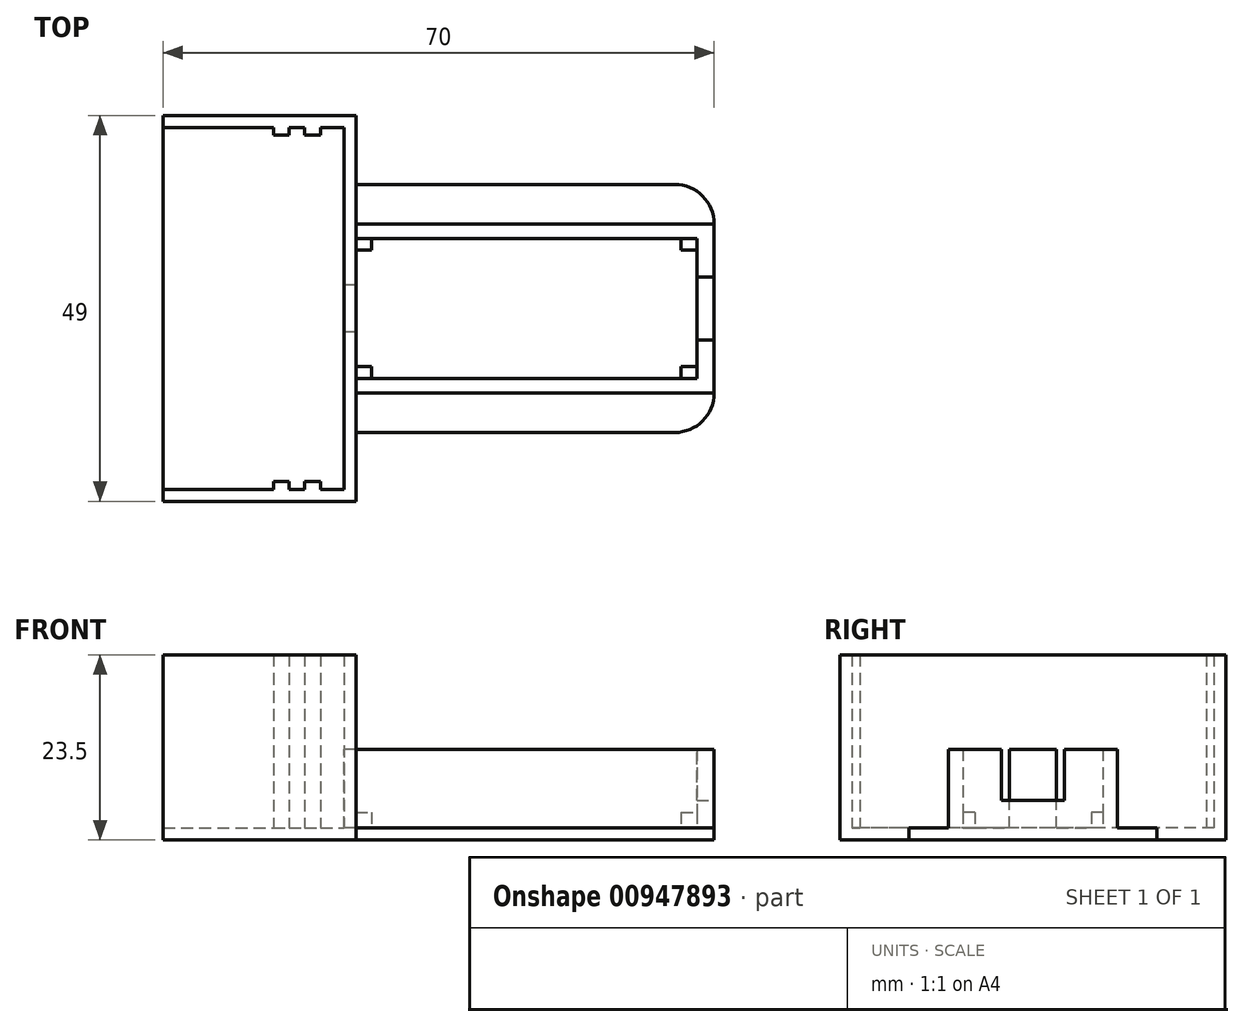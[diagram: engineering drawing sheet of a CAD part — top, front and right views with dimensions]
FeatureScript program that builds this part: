
annotation { "Feature Type Name" : "Feature", "Feature Type Description" : "" }
export const myFeature = defineFeature(function(context is Context, id is Id, definition is map)
    precondition{}
    {
        {
            var Q0;
            Q0=qCreatedBy(makeId("Top.planeOp"),FACE);
            var sketch = newSketch(context, id + "F0", { "sketchPlane" : qUnion([Q0])});
            skLineSegment(sketch, "E0.bottom", {"start": v(0, 24.5) * mm, "end": v(-23, 24.5) * mm});
            skLineSegment(sketch, "E0.top", {"start": v(0, -24.5) * mm, "end": v(-23, -24.5) * mm});
            skLineSegment(sketch, "E0.left", {"start": v(0, 24.5) * mm, "end": v(0, -24.5) * mm});
            skLineSegment(sketch, "E0.right", {"start": v(-23, 24.5) * mm, "end": v(-23, -24.5) * mm});
            skSolve(sketch);
        }
        {
            var Q0;
            Q0 = qSketchRegion(id + "F0", true);
            extrude(context, id + "F1", {"entities" : qUnion([Q0]), "depth" : 1.5 * mm, "offsetDistance" : 25 * mm});
        }
        {
            var Q0;
            Q0=makeQuery(id+"F1.opExtrude","CAP_FACE",FACE,{"disambiguationData":[OSD([sQuery(id+"F0.wireOp",EDGE,"E0.bottom"),sQuery(id+"F0.wireOp",EDGE,"E0.top"),sQuery(id+"F0.wireOp",EDGE,"E0.left"),sQuery(id+"F0.wireOp",EDGE,"E0.right")])],"isStart":false});
            var sketch = newSketch(context, id + "F2", { "sketchPlane" : qUnion([Q0])});
            skLineSegment(sketch, "E1.bottom", {"start": v(-23, 24.5) * mm, "end": v(0, 24.5) * mm});
            skLineSegment(sketch, "E1.top", {"start": v(-23, 23) * mm, "end": v(0, 23) * mm});
            skLineSegment(sketch, "E1.left", {"start": v(-23, 24.5) * mm, "end": v(-23, 23) * mm});
            skLineSegment(sketch, "E1.right", {"start": v(0, 24.5) * mm, "end": v(0, 23) * mm});
            skLineSegment(sketch, "E2.bottom", {"start": v(-23, -23) * mm, "end": v(0, -23) * mm});
            skLineSegment(sketch, "E2.top", {"start": v(-23, -24.5) * mm, "end": v(0, -24.5) * mm});
            skLineSegment(sketch, "E2.left", {"start": v(-23, -23) * mm, "end": v(-23, -24.5) * mm});
            skLineSegment(sketch, "E2.right", {"start": v(0, -23) * mm, "end": v(0, -24.5) * mm});
            skSolve(sketch);
        }
        {
            var Q0;
            Q0=makeQuery(id+"F2.imprint","IMPRINT",FACE,{"disambiguationData":[TD([[makeQuery(id+"F2.imprint","IMPRINT",EDGE,{"derivedFrom":sQuery(id+"F2.wireOp",EDGE,"E1.bottom")}),1.0]])]});
            var Q1;
            Q1=makeQuery(id+"F2.imprint","IMPRINT",FACE,{"disambiguationData":[TD([[makeQuery(id+"F2.imprint","IMPRINT",EDGE,{"derivedFrom":sQuery(id+"F2.wireOp",EDGE,"E2.bottom")}),-1.0]])]});
            extrude(context, id + "F3", {"entities" : qUnion([Q0, Q1]), "operationType" : NewBodyOperationType.ADD, "depth" : 22 * mm, "offsetDistance" : 25 * mm});
        }
        {
            var Q0;
            Q0=makeQuery(id+"F1.opExtrude","CAP_FACE",FACE,{"disambiguationData":[OSD([sQuery(id+"F0.wireOp",EDGE,"E0.bottom"),sQuery(id+"F0.wireOp",EDGE,"E0.top"),sQuery(id+"F0.wireOp",EDGE,"E0.left"),sQuery(id+"F0.wireOp",EDGE,"E0.right")])],"isStart":false});
            var sketch = newSketch(context, id + "F4", { "sketchPlane" : qUnion([Q0])});
            skLineSegment(sketch, "E3.bottom", {"start": v(-5, 23) * mm, "end": v(-3, 23) * mm});
            skLineSegment(sketch, "E3.top", {"start": v(-5, 22) * mm, "end": v(-3, 22) * mm});
            skLineSegment(sketch, "E3.left", {"start": v(-5, 23) * mm, "end": v(-5, 22) * mm});
            skLineSegment(sketch, "E3.right", {"start": v(-3, 23) * mm, "end": v(-3, 22) * mm});
            skLineSegment(sketch, "E4.bottom", {"start": v(-3, -23) * mm, "end": v(-5, -23) * mm});
            skLineSegment(sketch, "E4.top", {"start": v(-3, -22) * mm, "end": v(-5, -22) * mm});
            skLineSegment(sketch, "E4.left", {"start": v(-3, -23) * mm, "end": v(-3, -22) * mm});
            skLineSegment(sketch, "E4.right", {"start": v(-5, -23) * mm, "end": v(-5, -22) * mm});
            skLineSegment(sketch, "E5.bottom", {"start": v(-7, -23) * mm, "end": v(-9, -23) * mm});
            skLineSegment(sketch, "E5.top", {"start": v(-7, -22) * mm, "end": v(-9, -22) * mm});
            skLineSegment(sketch, "E5.left", {"start": v(-7, -23) * mm, "end": v(-7, -22) * mm});
            skLineSegment(sketch, "E5.right", {"start": v(-9, -23) * mm, "end": v(-9, -22) * mm});
            skLineSegment(sketch, "E6.bottom", {"start": v(-9, 23) * mm, "end": v(-7, 23) * mm});
            skLineSegment(sketch, "E6.top", {"start": v(-9, 22) * mm, "end": v(-7, 22) * mm});
            skLineSegment(sketch, "E6.left", {"start": v(-9, 23) * mm, "end": v(-9, 22) * mm});
            skLineSegment(sketch, "E6.right", {"start": v(-7, 23) * mm, "end": v(-7, 22) * mm});
            skSolve(sketch);
        }
        {
            var Q0;
            Q0=makeQuery(id+"F4.imprint","IMPRINT",FACE,{"disambiguationData":[TD([[makeQuery(id+"F4.imprint","IMPRINT",EDGE,{"derivedFrom":sQuery(id+"F4.wireOp",EDGE,"E3.bottom")}),-1.0]])]});
            var Q1;
            Q1=makeQuery(id+"F4.imprint","IMPRINT",FACE,{"disambiguationData":[TD([[makeQuery(id+"F4.imprint","IMPRINT",EDGE,{"derivedFrom":sQuery(id+"F4.wireOp",EDGE,"E5.bottom")}),1.0]])]});
            var Q2;
            Q2=makeQuery(id+"F4.imprint","IMPRINT",FACE,{"disambiguationData":[TD([[makeQuery(id+"F4.imprint","IMPRINT",EDGE,{"derivedFrom":sQuery(id+"F4.wireOp",EDGE,"E4.bottom")}),1.0]])]});
            var Q3;
            Q3=makeQuery(id+"F4.imprint","IMPRINT",FACE,{"disambiguationData":[TD([[makeQuery(id+"F4.imprint","IMPRINT",EDGE,{"derivedFrom":sQuery(id+"F4.wireOp",EDGE,"E6.bottom")}),-1.0]])]});
            extrude(context, id + "F5", {"entities" : qUnion([Q0, Q1, Q2, Q3]), "operationType" : NewBodyOperationType.ADD, "depth" : 22 * mm, "offsetDistance" : 25 * mm});
        }
        {
            var Q0;
            Q0=qCreatedBy(makeId("Top.planeOp"),FACE);
            var sketch = newSketch(context, id + "F6", { "sketchPlane" : qUnion([Q0])});
            skLineSegment(sketch, "E7.bottom", {"start": v(0, 10.75) * mm, "end": v(47, 10.75) * mm});
            skLineSegment(sketch, "E7.top", {"start": v(0, -10.75) * mm, "end": v(47, -10.75) * mm});
            skLineSegment(sketch, "E7.left", {"start": v(0, 10.75) * mm, "end": v(0, -10.75) * mm});
            skLineSegment(sketch, "E7.right", {"start": v(47, 10.75) * mm, "end": v(47, -10.75) * mm});
            skSolve(sketch);
        }
        {
            var Q0;
            Q0 = qSketchRegion(id + "F6", true);
            extrude(context, id + "F7", {"entities" : qUnion([Q0]), "operationType" : NewBodyOperationType.ADD, "depth" : 1.5 * mm, "offsetDistance" : 25 * mm});
        }
        {
            var Q0;
            Q0=qCreatedBy(makeId("Top.planeOp"),FACE);
            var sketch = newSketch(context, id + "F8", { "sketchPlane" : qUnion([Q0])});
            skLineSegment(sketch, "E8.bottom", {"start": v(0, 24.5) * mm, "end": v(1.5, 24.5) * mm});
            skLineSegment(sketch, "E8.top", {"start": v(0, -24.5) * mm, "end": v(1.5, -24.5) * mm});
            skLineSegment(sketch, "E8.left", {"start": v(0, 24.5) * mm, "end": v(0, -24.5) * mm});
            skLineSegment(sketch, "E8.right", {"start": v(1.5, 24.5) * mm, "end": v(1.5, -24.5) * mm});
            skSolve(sketch);
        }
        {
            var Q0;
            Q0 = qSketchRegion(id + "F8", true);
            extrude(context, id + "F9", {"entities" : qUnion([Q0]), "operationType" : NewBodyOperationType.ADD, "depth" : 23.5 * mm, "offsetDistance" : 25 * mm});
        }
        {
            var Q0;
            {var subQ0=sQuery(id+"F6.wireOp",EDGE,"E7.bottom");var subQ1=sQuery(id+"F6.wireOp",EDGE,"E7.right");var subQ2=sQuery(id+"F6.wireOp",EDGE,"E7.top");Q0=makeQuery(id+"F9.boolean.opBoolean","SPLIT",FACE,{"disambiguationData":[TD([makeQuery(id+"F7.opExtrude","SWEPT_FACE",FACE,{"disambiguationData":[OSD([subQ0])]})])],"derivedFrom":makeQuery(id+"F7.boolean.opBoolean","MERGE",FACE,{"derivedFrom":[makeQuery(id+"F1.opExtrude","CAP_FACE",FACE,{"disambiguationData":[OSD([sQuery(id+"F0.wireOp",EDGE,"E0.bottom"),sQuery(id+"F0.wireOp",EDGE,"E0.top"),sQuery(id+"F0.wireOp",EDGE,"E0.left"),sQuery(id+"F0.wireOp",EDGE,"E0.right")])],"isStart":false}),makeQuery(id+"F7.opExtrude","CAP_FACE",FACE,{"disambiguationData":[OSD([subQ0,subQ2,sQuery(id+"F6.wireOp",EDGE,"E7.left"),subQ1])],"isStart":false})]})});}
            var sketch = newSketch(context, id + "F10", { "sketchPlane" : qUnion([Q0])});
            skLineSegment(sketch, "E9.bottom", {"start": v(1.5, 8.9) * mm, "end": v(44.8, 8.9) * mm});
            skLineSegment(sketch, "E9.top", {"start": v(1.5, -8.9) * mm, "end": v(44.8, -8.9) * mm});
            skLineSegment(sketch, "E9.left", {"start": v(1.5, 8.9) * mm, "end": v(1.5, -8.9) * mm});
            skLineSegment(sketch, "E9.right", {"start": v(44.8, 8.9) * mm, "end": v(44.8, -8.9) * mm});
            skSolve(sketch);
        }
        {
            var Q0;
            {var subQ2=sQuery(id+"F10.wireOp",EDGE,"E9.bottom");Q0=makeQuery(id+"F10.imprint","IMPRINT",FACE,{"disambiguationData":[TD([[makeQuery(id+"F10.imprint","IMPRINT",EDGE,{"derivedFrom":subQ2}),1.0]])]});}
            extrude(context, id + "F11", {"entities" : qUnion([Q0]), "operationType" : NewBodyOperationType.ADD, "depth" : 10 * mm, "offsetDistance" : 25 * mm});
        }
        {
            var Q0;
            Q0=makeQuery(id+"F9.opExtrude","SWEPT_FACE",FACE,{"disambiguationData":[OSD([sQuery(id+"F8.wireOp",EDGE,"E8.left")])]});
            var sketch = newSketch(context, id + "F12", { "sketchPlane" : qUnion([Q0])});
            skLineSegment(sketch, "E10.bottom", {"start": v(-3, 1.5) * mm, "end": v(3, 1.5) * mm});
            skLineSegment(sketch, "E10.top", {"start": v(-3, 11.5) * mm, "end": v(3, 11.5) * mm});
            skLineSegment(sketch, "E10.left", {"start": v(-3, 1.5) * mm, "end": v(-3, 11.5) * mm});
            skLineSegment(sketch, "E10.right", {"start": v(3, 1.5) * mm, "end": v(3, 11.5) * mm});
            skSolve(sketch);
        }
        {
            var Q0;
            Q0 = qSketchRegion(id + "F12", true);
            extrude(context, id + "F13", {"entities" : qUnion([Q0]), "operationType" : NewBodyOperationType.REMOVE, "endBound" : BoundingType.UP_TO_NEXT, "oppositeDirection" : true, "depth" : 25 * mm, "offsetDistance" : 25 * mm});
        }
        {
            var Q0;
            {var subQ0=sQuery(id+"F6.wireOp",EDGE,"E7.bottom");var subQ1=sQuery(id+"F6.wireOp",EDGE,"E7.right");var subQ2=sQuery(id+"F6.wireOp",EDGE,"E7.top");var subQ3=sQuery(id+"F0.wireOp",EDGE,"E0.right");var subQ4=makeQuery(id+"F7.boolean.opBoolean","MERGE",FACE,{"derivedFrom":[makeQuery(id+"F1.opExtrude","CAP_FACE",FACE,{"disambiguationData":[OSD([sQuery(id+"F0.wireOp",EDGE,"E0.bottom"),sQuery(id+"F0.wireOp",EDGE,"E0.top"),sQuery(id+"F0.wireOp",EDGE,"E0.left"),subQ3])],"isStart":false}),makeQuery(id+"F7.opExtrude","CAP_FACE",FACE,{"disambiguationData":[OSD([subQ0,subQ2,sQuery(id+"F6.wireOp",EDGE,"E7.left"),subQ1])],"isStart":false})]});Q0=makeQuery(id+"F13.boolean.opBoolean","MERGE",FACE,{"derivedFrom":[makeQuery(id+"F9.boolean.opBoolean","SPLIT",FACE,{"disambiguationData":[TD([makeQuery(id+"F1.opExtrude","SWEPT_FACE",FACE,{"disambiguationData":[OSD([subQ3])]})])],"derivedFrom":subQ4}),makeQuery(id+"F9.boolean.opBoolean","SPLIT",FACE,{"disambiguationData":[TD([makeQuery(id+"F7.opExtrude","SWEPT_FACE",FACE,{"disambiguationData":[OSD([subQ0])]})])],"derivedFrom":subQ4})],"fromTools":[makeQuery(id+"F13.opExtrude","SWEPT_FACE",FACE,{"disambiguationData":[OSD([sQuery(id+"F12.wireOp",EDGE,"E10.bottom")])]})]});}
            var sketch = newSketch(context, id + "F14", { "sketchPlane" : qUnion([Q0])});
            skLineSegment(sketch, "E11.bottom", {"start": v(1.5, 7.4) * mm, "end": v(3.5, 7.4) * mm});
            skLineSegment(sketch, "E11.top", {"start": v(1.5, 8.9) * mm, "end": v(3.5, 8.9) * mm});
            skLineSegment(sketch, "E11.left", {"start": v(1.5, 7.4) * mm, "end": v(1.5, 8.9) * mm});
            skLineSegment(sketch, "E11.right", {"start": v(3.5, 7.4) * mm, "end": v(3.5, 8.9) * mm});
            skLineSegment(sketch, "E12.bottom", {"start": v(1.5, -7.4) * mm, "end": v(3.5, -7.4) * mm});
            skLineSegment(sketch, "E12.top", {"start": v(1.5, -8.9) * mm, "end": v(3.5, -8.9) * mm});
            skLineSegment(sketch, "E12.left", {"start": v(1.5, -7.4) * mm, "end": v(1.5, -8.9) * mm});
            skLineSegment(sketch, "E12.right", {"start": v(3.5, -7.4) * mm, "end": v(3.5, -8.9) * mm});
            skLineSegment(sketch, "E13.bottom", {"start": v(42.8, 8.9) * mm, "end": v(44.8, 8.9) * mm});
            skLineSegment(sketch, "E13.top", {"start": v(42.8, 7.4) * mm, "end": v(44.8, 7.4) * mm});
            skLineSegment(sketch, "E13.left", {"start": v(42.8, 8.9) * mm, "end": v(42.8, 7.4) * mm});
            skLineSegment(sketch, "E13.right", {"start": v(44.8, 8.9) * mm, "end": v(44.8, 7.4) * mm});
            skLineSegment(sketch, "E14.bottom", {"start": v(42.8, -8.9) * mm, "end": v(44.8, -8.9) * mm});
            skLineSegment(sketch, "E14.top", {"start": v(42.8, -7.4) * mm, "end": v(44.8, -7.4) * mm});
            skLineSegment(sketch, "E14.left", {"start": v(42.8, -8.9) * mm, "end": v(42.8, -7.4) * mm});
            skLineSegment(sketch, "E14.right", {"start": v(44.8, -8.9) * mm, "end": v(44.8, -7.4) * mm});
            skSolve(sketch);
        }
        {
            var Q0;
            Q0 = qSketchRegion(id + "F14", true);
            extrude(context, id + "F15", {"entities" : qUnion([Q0]), "operationType" : NewBodyOperationType.ADD, "depth" : 2 * mm, "offsetDistance" : 25 * mm});
        }
        {
            var Q0;
            {var subQ0=sQuery(id+"F6.wireOp",EDGE,"E7.right");Q0=makeQuery(id+"F11.boolean.opBoolean","MERGE",FACE,{"derivedFrom":[makeQuery(id+"F7.opExtrude","SWEPT_FACE",FACE,{"disambiguationData":[OSD([subQ0])]}),makeQuery(id+"F11.opExtrude","SWEPT_FACE",FACE,{"disambiguationData":[OSD([subQ0])]})]});}
            var sketch = newSketch(context, id + "F16", { "sketchPlane" : qUnion([Q0])});
            skLineSegment(sketch, "E15.bottom", {"start": v(-4, 11.5) * mm, "end": v(4, 11.5) * mm});
            skLineSegment(sketch, "E15.top", {"start": v(-4, 5) * mm, "end": v(4, 5) * mm});
            skLineSegment(sketch, "E15.left", {"start": v(-4, 11.5) * mm, "end": v(-4, 5) * mm});
            skLineSegment(sketch, "E15.right", {"start": v(4, 11.5) * mm, "end": v(4, 5) * mm});
            skSolve(sketch);
        }
        {
            var Q0;
            Q0=makeQuery(id+"F16.imprint","IMPRINT",FACE,{"disambiguationData":[TD([[makeQuery(id+"F16.imprint","IMPRINT",EDGE,{"derivedFrom":sQuery(id+"F16.wireOp",EDGE,"E15.bottom")}),1.0]])]});
            extrude(context, id + "F17", {"entities" : qUnion([Q0]), "operationType" : NewBodyOperationType.REMOVE, "endBound" : BoundingType.UP_TO_NEXT, "oppositeDirection" : true, "depth" : 25 * mm, "offsetDistance" : 25 * mm});
        }
        {
            var Q0;
            {var subQ0=sQuery(id+"F6.wireOp",EDGE,"E7.bottom");Q0=makeQuery(id+"F11.boolean.opBoolean","MERGE",FACE,{"derivedFrom":[makeQuery(id+"F7.opExtrude","SWEPT_FACE",FACE,{"disambiguationData":[OSD([subQ0])]}),makeQuery(id+"F11.opExtrude","SWEPT_FACE",FACE,{"disambiguationData":[OSD([subQ0])]})]});}
            var sketch = newSketch(context, id + "F18", { "sketchPlane" : qUnion([Q0])});
            skLineSegment(sketch, "E16.bottom", {"start": v(-47, 0) * mm, "end": v(-1.5, 0) * mm});
            skLineSegment(sketch, "E16.top", {"start": v(-47, 1.5) * mm, "end": v(-1.5, 1.5) * mm});
            skLineSegment(sketch, "E16.left", {"start": v(-47, 0) * mm, "end": v(-47, 1.5) * mm});
            skLineSegment(sketch, "E16.right", {"start": v(-1.5, 0) * mm, "end": v(-1.5, 1.5) * mm});
            skSolve(sketch);
        }
        {
            var Q0;
            Q0=makeQuery(id+"F18.imprint","IMPRINT",FACE,{"disambiguationData":[TD([[makeQuery(id+"F18.imprint","IMPRINT",EDGE,{"derivedFrom":sQuery(id+"F18.wireOp",EDGE,"E16.bottom")}),-1.0]])]});
            extrude(context, id + "F19", {"entities" : qUnion([Q0]), "operationType" : NewBodyOperationType.ADD, "depth" : 5 * mm, "offsetDistance" : 25 * mm});
        }
        {
            var Q0;
            {var subQ0=sQuery(id+"F6.wireOp",EDGE,"E7.top");Q0=makeQuery(id+"F11.boolean.opBoolean","MERGE",FACE,{"derivedFrom":[makeQuery(id+"F7.opExtrude","SWEPT_FACE",FACE,{"disambiguationData":[OSD([subQ0])]}),makeQuery(id+"F11.opExtrude","SWEPT_FACE",FACE,{"disambiguationData":[OSD([subQ0])]})]});}
            var sketch = newSketch(context, id + "F20", { "sketchPlane" : qUnion([Q0])});
            skLineSegment(sketch, "E17.bottom", {"start": v(1.5, 1.5) * mm, "end": v(47, 1.5) * mm});
            skLineSegment(sketch, "E17.top", {"start": v(1.5, 0) * mm, "end": v(47, 0) * mm});
            skLineSegment(sketch, "E17.left", {"start": v(1.5, 1.5) * mm, "end": v(1.5, 0) * mm});
            skLineSegment(sketch, "E17.right", {"start": v(47, 1.5) * mm, "end": v(47, 0) * mm});
            skSolve(sketch);
        }
        {
            var Q0;
            Q0=makeQuery(id+"F20.imprint","IMPRINT",FACE,{"disambiguationData":[TD([[makeQuery(id+"F20.imprint","IMPRINT",EDGE,{"derivedFrom":sQuery(id+"F20.wireOp",EDGE,"E17.bottom")}),-1.0]])]});
            extrude(context, id + "F21", {"entities" : qUnion([Q0]), "operationType" : NewBodyOperationType.ADD, "depth" : 5 * mm, "offsetDistance" : 25 * mm});
        }
        {
            var Q0;
            Q0=makeQuery(id+"F19.opExtrude","CAP_EDGE",EDGE,{"disambiguationData":[OSD([sQuery(id+"F18.wireOp",EDGE,"E16.left")])],"isStart":false});
            var Q1;
            Q1=makeQuery(id+"F19.opExtrude","CAP_EDGE",EDGE,{"disambiguationData":[OSD([sQuery(id+"F18.wireOp",EDGE,"E16.right")])],"isStart":false});
            var Q2;
            Q2=makeQuery(id+"F21.opExtrude","CAP_EDGE",EDGE,{"disambiguationData":[OSD([sQuery(id+"F20.wireOp",EDGE,"E17.right")])],"isStart":false});
            var Q3;
            Q3=makeQuery(id+"F21.opExtrude","CAP_EDGE",EDGE,{"disambiguationData":[OSD([sQuery(id+"F20.wireOp",EDGE,"E17.left")])],"isStart":false});
            fillet(context, id + "F22", {"entities" : qUnion([Q0, Q1, Q2, Q3]), "radius" : 5 * mm, "tangentPropagation" : true, "allowEdgeOverflow" : false});
        }
    });
